# Revit family: EKF_EE_ШирокаяВертикальнаяРейкаFORT_PROxima
name_source: partatom
category: Электрооборудование
units: mm (PartAtom-declared; Revit-internal decimal feet)

## family parameters
Всегда вертикально = Нет
На основе рабочей плоскости = Да
Общий = Да
При загрузке вырезать с полостями = Нет
Размер круглого соединителя = Использовать диаметр
Тип детали = Силовой щит
Точка расчета площади = Нет

## types (3) — shared parameters
ADSK_Единица измерения = шт.
ADSK_Завод-изготовитель = EKF
ADSK_Количество = 1
ADSK_Марка = Широкая вертикальная рейка FORT
ADSK_Материал = Сталь_Оцинкованная
ADSK_Обозначение = Широкая вертикальная рейка FORT
ADSK_Размер_Глубина = 22 мм
ADSK_Размер_Ширина = 50 мм
t = 1.5 мм
Изготовитель = EKF
Серия номенклатуры = PROxima
Степень защиты IP = -
ТВ = EKF_2
Тип установки = -
zero-valued in all types: ADSK_Масса, Отметка по умолчанию

## per-type parameters (varying)
| type | ADSK_Код изделия | ADSK_Размер_Высота | Тип |
| Широкая вертикальная рейка FORT для корпуса высотой 1800 (2шт.) EKF PROxima | FVR18S | 1764 мм | 309 мм |
| Широкая вертикальная рейка FORT для корпуса высотой 2000 (2шт.) EKF PROxima | FVR20S | 1964 мм | 310 мм |
| Широкая вертикальная рейка FORT для корпуса высотой 2200 (2шт.) EKF PROxima | FVR22S | 2164 мм | 311 мм |

note: column(s) folded — value = type name in every type: ADSK_Наименование
